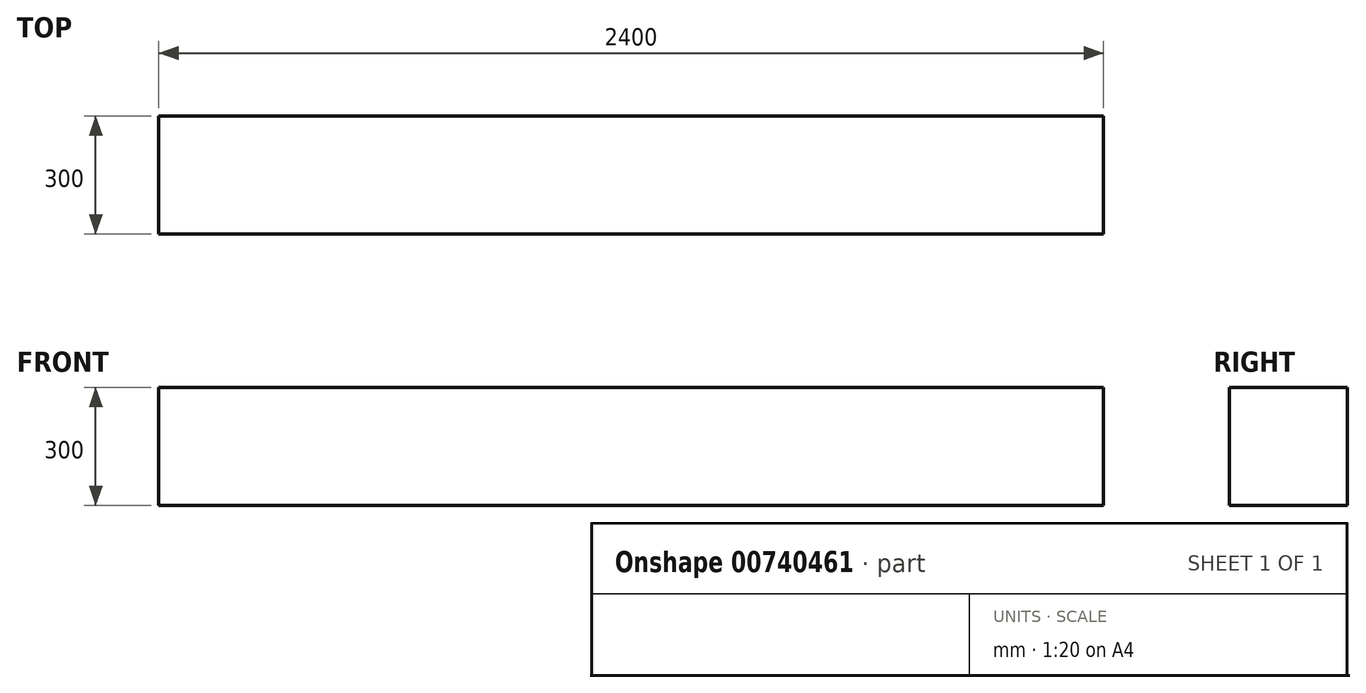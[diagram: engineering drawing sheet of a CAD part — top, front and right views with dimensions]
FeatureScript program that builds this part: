
annotation { "Feature Type Name" : "Feature", "Feature Type Description" : "" }
export const myFeature = defineFeature(function(context is Context, id is Id, definition is map)
    precondition{}
    {
        {
            var Q0;
            Q0=qCreatedBy(makeId("Top.planeOp"),FACE);
            var sketch = newSketch(context, id + "F0", { "sketchPlane" : qUnion([Q0])});
            skLineSegment(sketch, "E0.bottom", {"start": v(-1200, 150) * mm, "end": v(1200, 150) * mm});
            skLineSegment(sketch, "E0.top", {"start": v(-1200, -150) * mm, "end": v(1200, -150) * mm});
            skLineSegment(sketch, "E0.left", {"start": v(-1200, 150) * mm, "end": v(-1200, -150) * mm});
            skLineSegment(sketch, "E0.right", {"start": v(1200, 150) * mm, "end": v(1200, -150) * mm});
            skPoint(sketch, "E0.middle", {"position": v(0, 0) * mm});
            skSolve(sketch);
        }
        {
            var Q0;
            Q0=makeQuery(id+"F0.imprint","IMPRINT",FACE,{"disambiguationData":[TD([[makeQuery(id+"F0.imprint","IMPRINT",EDGE,{"derivedFrom":sQuery(id+"F0.wireOp",EDGE,"E0.bottom")}),-1.0]])]});
            extrude(context, id + "F1", {"entities" : qUnion([Q0]), "depth" : 300 * mm, "offsetDistance" : 25.4 * mm});
        }
    });
